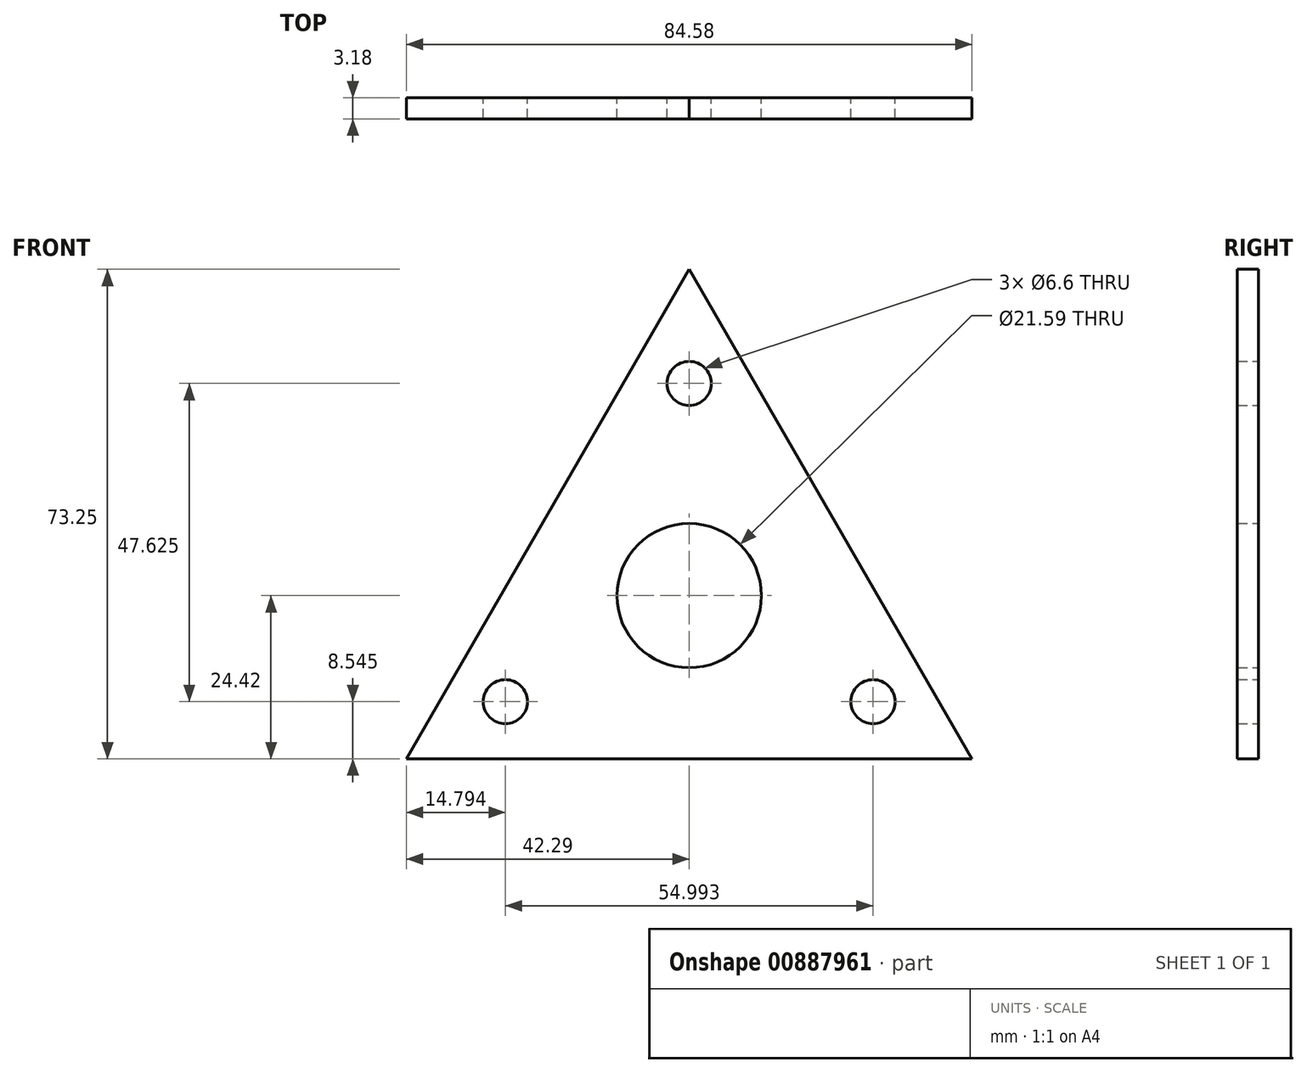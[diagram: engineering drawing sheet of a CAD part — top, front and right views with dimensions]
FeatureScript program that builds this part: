
annotation { "Feature Type Name" : "Feature", "Feature Type Description" : "" }
export const myFeature = defineFeature(function(context is Context, id is Id, definition is map)
    precondition{}
    {
        {
            var Q0;
            Q0=qCreatedBy(makeId("Front.planeOp"),FACE);
            var sketch = newSketch(context, id + "F0", { "sketchPlane" : qUnion([Q0])});
            skCircle(sketch, "E0", {"center": v(0, 0) * mm, "radius": 10.8 * mm});
            skCircle(sketch, "E1.cCircle", {"center": v(0, 0) * mm, "radius": 24.42 * mm, "construction": true});
            skLineSegment(sketch, "E1.0", {"start": v(0, 48.83) * mm, "end": v(42.3, -24.42) * mm});
            skLineSegment(sketch, "E1.1", {"start": v(42.3, -24.42) * mm, "end": v(-42.3, -24.42) * mm});
            skLineSegment(sketch, "E1.2", {"start": v(-42.3, -24.42) * mm, "end": v(0, 48.83) * mm});
            skPoint(sketch, "E1.0.midPoint", {"position": v(21.15, 12.2) * mm});
            skLineSegment(sketch, "E2", {"start": v(0, 0) * mm, "end": v(0, 98.14) * mm, "construction": true});
            skCircle(sketch, "E3", {"center": v(0, 0) * mm, "radius": 15.75 * mm, "construction": true});
            skCircle(sketch, "E4", {"center": v(0, 31.75) * mm, "radius": 3.3 * mm});
            skCircle(sketch, "E5.1.0", {"center": v(-27.5, -15.87) * mm, "radius": 3.3 * mm});
            skCircle(sketch, "E5.2.0", {"center": v(27.5, -15.88) * mm, "radius": 3.3 * mm});
            skSolve(sketch);
        }
        {
            var Q0;
            Q0 = qSketchRegion(id + "F0", true);
            extrude(context, id + "F1", {"entities" : qUnion([Q0]), "depth" : 3.17 * mm, "offsetDistance" : 25.4 * mm});
        }
    });
